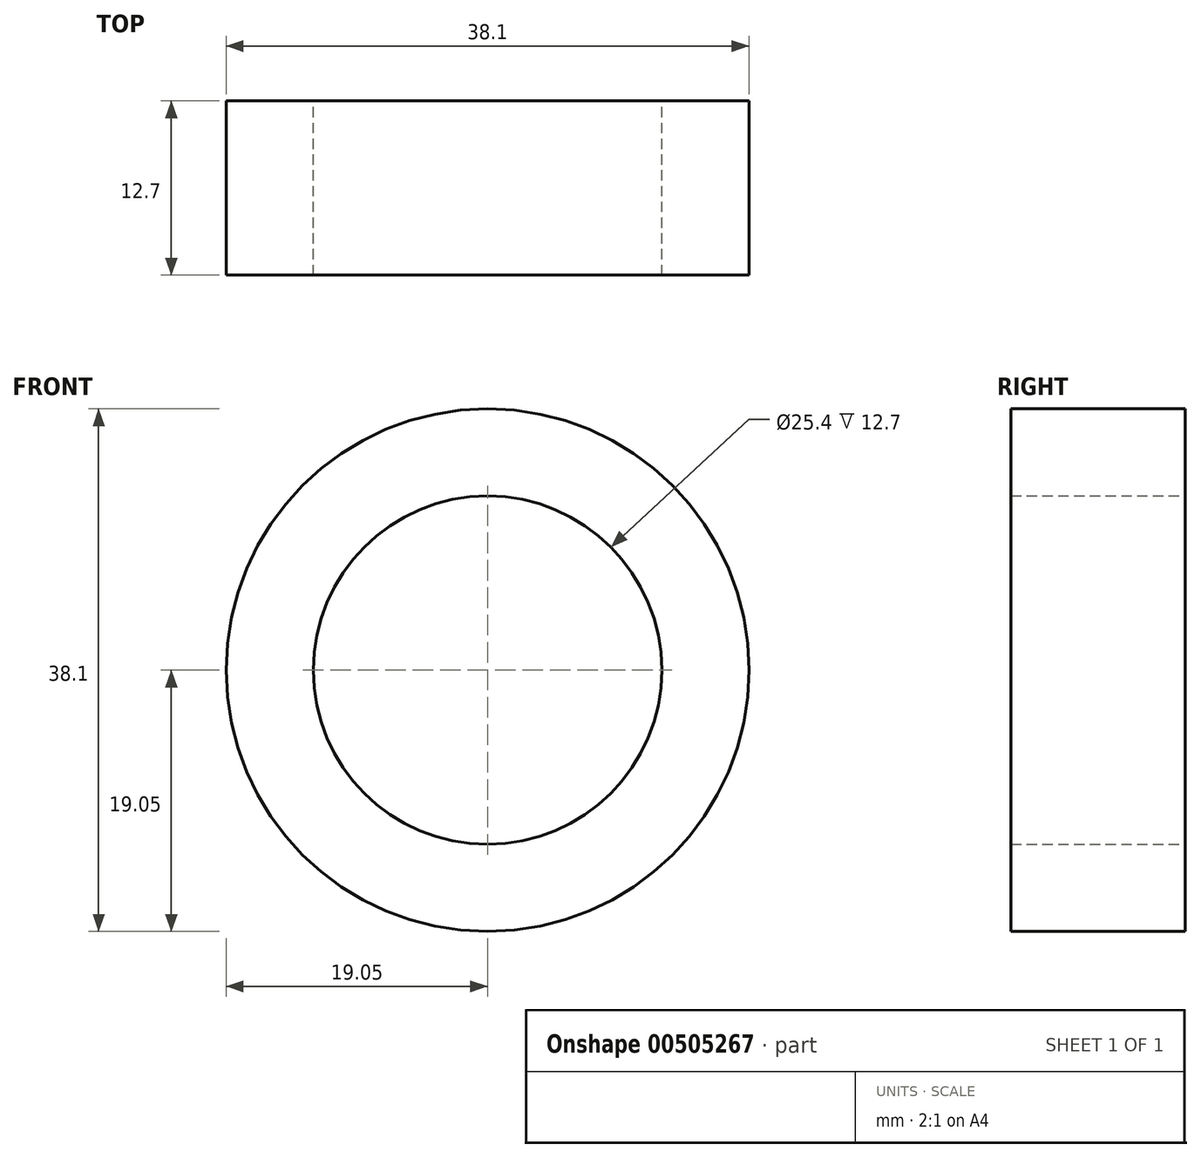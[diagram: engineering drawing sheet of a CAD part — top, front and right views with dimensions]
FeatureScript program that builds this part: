
annotation { "Feature Type Name" : "Feature", "Feature Type Description" : "" }
export const myFeature = defineFeature(function(context is Context, id is Id, definition is map)
    precondition{}
    {
        {
            var Q0;
            Q0=qCreatedBy(makeId("Front.planeOp"),FACE);
            var sketch = newSketch(context, id + "F0", { "sketchPlane" : qUnion([Q0])});
            skCircle(sketch, "E0", {"center": v(0, 0) * mm, "radius": 19.05 * mm});
            skCircle(sketch, "E1", {"center": v(0, 0) * mm, "radius": 12.7 * mm});
            skSolve(sketch);
        }
        {
            var Q0;
            Q0=makeQuery(id+"F0.imprint","IMPRINT",FACE,{"disambiguationData":[TD([[makeQuery(id+"F0.imprint","IMPRINT",EDGE,{"derivedFrom":sQuery(id+"F0.wireOp",EDGE,"E0")}),1.0]])]});
            extrude(context, id + "F1", {"entities" : qUnion([Q0]), "depth" : 12.7 * mm});
        }
    });
